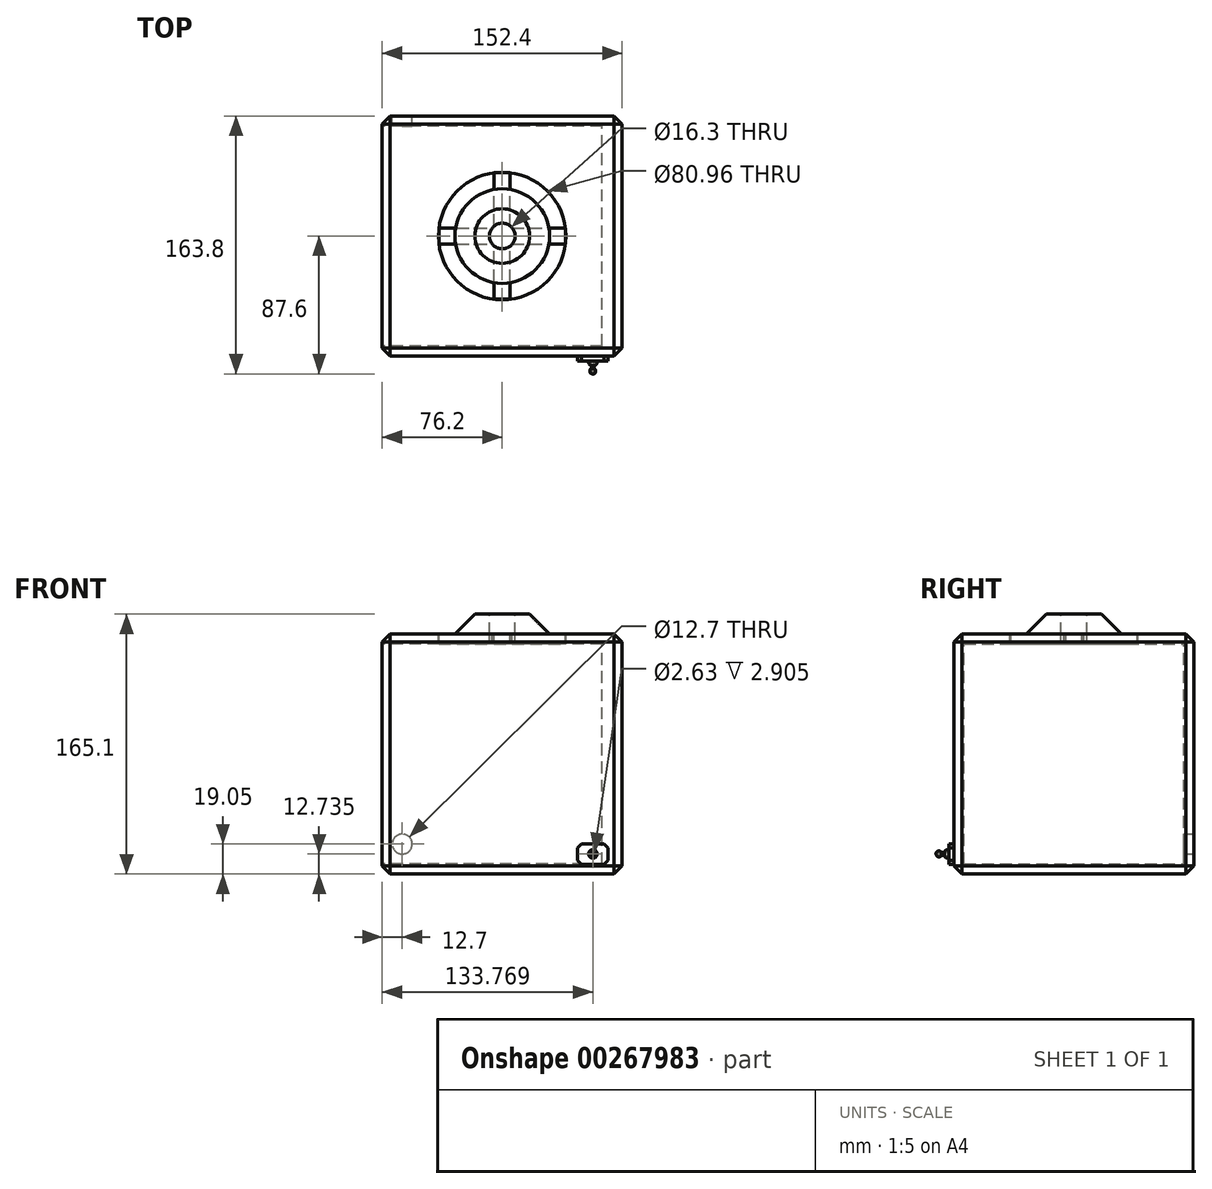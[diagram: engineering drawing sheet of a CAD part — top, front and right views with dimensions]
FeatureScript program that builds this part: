
annotation { "Feature Type Name" : "Feature", "Feature Type Description" : "" }
export const myFeature = defineFeature(function(context is Context, id is Id, definition is map)
    precondition{}
    {
        {
            var Q0;
            Q0=qCreatedBy(makeId("Top.planeOp"),FACE);
            var sketch = newSketch(context, id + "F0", { "sketchPlane" : qUnion([Q0])});
            skLineSegment(sketch, "E0.bottom", {"start": v(152.4, -152.4) * mm, "end": v(-152.4, -152.4) * mm});
            skLineSegment(sketch, "E0.top", {"start": v(152.4, 152.4) * mm, "end": v(-152.4, 152.4) * mm});
            skLineSegment(sketch, "E0.left", {"start": v(152.4, -152.4) * mm, "end": v(152.4, 152.4) * mm});
            skLineSegment(sketch, "E0.right", {"start": v(-152.4, -152.4) * mm, "end": v(-152.4, 152.4) * mm});
            skPoint(sketch, "E0.middle", {"position": v(0, 0) * mm});
            skSolve(sketch);
        }
        {
            var Q0;
            Q0=makeQuery(id+"F0.imprint","IMPRINT",FACE,{"disambiguationData":[TD([[makeQuery(id+"F0.imprint","IMPRINT",EDGE,{"derivedFrom":sQuery(id+"F0.wireOp",EDGE,"E0.bottom")}),-1.0]])]});
            extrude(context, id + "F1", {"entities" : qUnion([Q0]), "depth" : 304.8 * mm});
        }
        {
            var Q0;
            Q0=makeQuery(id+"F1.opExtrude","CAP_FACE",FACE,{"disambiguationData":[OSD([sQuery(id+"F0.wireOp",EDGE,"E0.bottom"),sQuery(id+"F0.wireOp",EDGE,"E0.top"),sQuery(id+"F0.wireOp",EDGE,"E0.left"),sQuery(id+"F0.wireOp",EDGE,"E0.right")])],"isStart":false});
            var sketch = newSketch(context, id + "F2", { "sketchPlane" : qUnion([Q0])});
            skCircle(sketch, "E1", {"center": v(0, 0) * mm, "radius": 80.96 * mm});
            skSolve(sketch);
        }
        {
            var Q0;
            Q0=makeQuery(id+"F1.opExtrude","SWEPT_FACE",FACE,{"disambiguationData":[OSD([sQuery(id+"F0.wireOp",EDGE,"E0.right")])]});
            var sketch = newSketch(context, id + "F3", { "sketchPlane" : qUnion([Q0])});
            skLineSegment(sketch, "E2.bottom", {"start": v(139.7, 12.7) * mm, "end": v(-139.7, 12.7) * mm});
            skLineSegment(sketch, "E2.top", {"start": v(139.7, 292.1) * mm, "end": v(-139.7, 292.1) * mm});
            skLineSegment(sketch, "E2.left", {"start": v(139.7, 12.7) * mm, "end": v(139.7, 292.1) * mm});
            skLineSegment(sketch, "E2.right", {"start": v(-139.7, 12.7) * mm, "end": v(-139.7, 292.1) * mm});
            skPoint(sketch, "E2.middle", {"position": v(0, 152.4) * mm});
            skSolve(sketch);
        }
        {
            var Q0;
            Q0=makeQuery(id+"F3.imprint","IMPRINT",FACE,{"disambiguationData":[TD([[makeQuery(id+"F3.imprint","IMPRINT",EDGE,{"derivedFrom":sQuery(id+"F3.wireOp",EDGE,"E2.bottom")}),-1.0]])]});
            extrude(context, id + "F4", {"entities" : qUnion([Q0]), "operationType" : NewBodyOperationType.REMOVE, "oppositeDirection" : true, "depth" : 279.4 * mm});
        }
        {
            var Q0;
            Q0=makeQuery(id+"F2.imprint","IMPRINT",FACE,{"disambiguationData":[TD([[makeQuery(id+"F2.imprint","IMPRINT",EDGE,{"derivedFrom":sQuery(id+"F2.wireOp",EDGE,"E1")}),1.0]])]});
            extrude(context, id + "F5", {"entities" : qUnion([Q0]), "operationType" : NewBodyOperationType.REMOVE, "oppositeDirection" : true, "depth" : 25.4 * mm});
        }
        {
            var Q0;
            Q0=makeQuery(id+"F1.opExtrude","SWEPT_FACE",FACE,{"disambiguationData":[OSD([sQuery(id+"F0.wireOp",EDGE,"E0.top")])]});
            var sketch = newSketch(context, id + "F6", { "sketchPlane" : qUnion([Q0])});
            skCircle(sketch, "E3", {"center": v(127, 38.1) * mm, "radius": 12.7 * mm});
            skSolve(sketch);
        }
        {
            var Q0;
            Q0=makeQuery(id+"F1.opExtrude","CAP_FACE",FACE,{"disambiguationData":[OSD([sQuery(id+"F0.wireOp",EDGE,"E0.bottom"),sQuery(id+"F0.wireOp",EDGE,"E0.top"),sQuery(id+"F0.wireOp",EDGE,"E0.left"),sQuery(id+"F0.wireOp",EDGE,"E0.right")])],"isStart":false});
            var sketch = newSketch(context, id + "F7", { "sketchPlane" : qUnion([Q0])});
            skCircle(sketch, "E4", {"center": v(0, 0) * mm, "radius": 60.08 * mm});
            skSolve(sketch);
        }
        {
            var Q0;
            Q0 = qSketchRegion(id + "F6", true);
            extrude(context, id + "F8", {"entities" : qUnion([Q0]), "operationType" : NewBodyOperationType.REMOVE, "endBound" : BoundingType.UP_TO_NEXT, "oppositeDirection" : true, "depth" : 25.4 * mm});
        }
        {
            var Q0;
            Q0=makeQuery(id+"F1.opExtrude","SWEPT_FACE",FACE,{"disambiguationData":[OSD([sQuery(id+"F0.wireOp",EDGE,"E0.bottom")])]});
            var sketch = newSketch(context, id + "F9", { "sketchPlane" : qUnion([Q0])});
            skLineSegment(sketch, "E5.bottom", {"start": v(134.19, 38.44) * mm, "end": v(95.34, 38.44) * mm});
            skLineSegment(sketch, "E5.top", {"start": v(134.19, 12.14) * mm, "end": v(95.34, 12.14) * mm});
            skLineSegment(sketch, "E5.left", {"start": v(134.19, 38.44) * mm, "end": v(134.19, 12.14) * mm});
            skLineSegment(sketch, "E5.right", {"start": v(95.34, 38.44) * mm, "end": v(95.34, 12.14) * mm});
            skSolve(sketch);
        }
        {
            var Q0;
            Q0 = qSketchRegion(id + "F9", true);
            extrude(context, id + "F10", {"entities" : qUnion([Q0]), "operationType" : NewBodyOperationType.ADD, "depth" : 6.35 * mm});
        }
        {
            var Q0;
            Q0=makeQuery(id+"F7.imprint","IMPRINT",FACE,{"disambiguationData":[TD([[makeQuery(id+"F7.imprint","IMPRINT",EDGE,{"derivedFrom":sQuery(id+"F7.wireOp",EDGE,"E4")}),1.0]])]});
            extrude(context, id + "F11", {"entities" : qUnion([Q0]), "depth" : 25.4 * mm});
        }
        {
            var Q0;
            Q0=makeQuery(id+"F10.opExtrude","SWEPT_EDGE",EDGE,{"disambiguationData":[OSD([sQuery(id+"F9.wireOp",EDGE,"E5.bottom"),sQuery(id+"F9.wireOp",EDGE,"E5.right")])]});
            var Q1;
            Q1=makeQuery(id+"F10.opExtrude","SWEPT_EDGE",EDGE,{"disambiguationData":[OSD([sQuery(id+"F9.wireOp",EDGE,"E5.top"),sQuery(id+"F9.wireOp",EDGE,"E5.left")])]});
            var Q2;
            Q2=makeQuery(id+"F10.opExtrude","SWEPT_EDGE",EDGE,{"disambiguationData":[OSD([sQuery(id+"F9.wireOp",EDGE,"E5.bottom"),sQuery(id+"F9.wireOp",EDGE,"E5.left")])]});
            var Q3;
            Q3=makeQuery(id+"F10.opExtrude","SWEPT_EDGE",EDGE,{"disambiguationData":[OSD([sQuery(id+"F9.wireOp",EDGE,"E5.top"),sQuery(id+"F9.wireOp",EDGE,"E5.right")])]});
            chamfer(context, id + "F12", {"entities" : qUnion([Q0, Q1, Q2, Q3]), "width" : 5.08 * mm, "tangentPropagation" : true});
        }
        {
            var Q0;
            Q0=makeQuery(id+"F11.opExtrude","CAP_FACE",FACE,{"disambiguationData":[OSD([sQuery(id+"F7.wireOp",EDGE,"E4")])],"isStart":false});
            chamfer(context, id + "F13", {"entities" : qUnion([Q0]), "width" : 25.4 * mm, "tangentPropagation" : true});
        }
        {
            var Q0;
            Q0=makeQuery(id+"F1.opExtrude","CAP_FACE",FACE,{"disambiguationData":[OSD([sQuery(id+"F0.wireOp",EDGE,"E0.bottom"),sQuery(id+"F0.wireOp",EDGE,"E0.top"),sQuery(id+"F0.wireOp",EDGE,"E0.left"),sQuery(id+"F0.wireOp",EDGE,"E0.right")])],"isStart":false});
            var sketch = newSketch(context, id + "F14", { "sketchPlane" : qUnion([Q0])});
            skLineSegment(sketch, "E6.bottom", {"start": v(10.16, -80.32) * mm, "end": v(-10.16, -80.32) * mm});
            skLineSegment(sketch, "E6.top", {"start": v(10.16, 80.32) * mm, "end": v(-10.16, 80.32) * mm});
            skLineSegment(sketch, "E6.left", {"start": v(10.16, -80.32) * mm, "end": v(10.16, 80.32) * mm});
            skLineSegment(sketch, "E6.right", {"start": v(-10.16, -80.32) * mm, "end": v(-10.16, 80.32) * mm});
            skPoint(sketch, "E6.middle", {"position": v(0, 0) * mm});
            skSolve(sketch);
        }
        {
            var Q0;
            Q0 = qSketchRegion(id + "F14", true);
            extrude(context, id + "F15", {"entities" : qUnion([Q0]), "oppositeDirection" : true, "depth" : 12.7 * mm});
        }
        {
            var Q0;
            Q0=makeQuery(id+"F1.opExtrude","CAP_FACE",FACE,{"disambiguationData":[OSD([sQuery(id+"F0.wireOp",EDGE,"E0.bottom"),sQuery(id+"F0.wireOp",EDGE,"E0.top"),sQuery(id+"F0.wireOp",EDGE,"E0.left"),sQuery(id+"F0.wireOp",EDGE,"E0.right")])],"isStart":false});
            var sketch = newSketch(context, id + "F16", { "sketchPlane" : qUnion([Q0])});
            skLineSegment(sketch, "E7.bottom", {"start": v(-80.32, 10.16) * mm, "end": v(80.32, 10.16) * mm});
            skLineSegment(sketch, "E7.top", {"start": v(-80.32, -10.16) * mm, "end": v(80.32, -10.16) * mm});
            skLineSegment(sketch, "E7.left", {"start": v(-80.32, 10.16) * mm, "end": v(-80.32, -10.16) * mm});
            skLineSegment(sketch, "E7.right", {"start": v(80.32, 10.16) * mm, "end": v(80.32, -10.16) * mm});
            skPoint(sketch, "E7.middle", {"position": v(0, 0) * mm});
            skSolve(sketch);
        }
        {
            var Q0;
            Q0=makeQuery(id+"F16.imprint","IMPRINT",FACE,{"disambiguationData":[TD([[makeQuery(id+"F16.imprint","IMPRINT",EDGE,{"derivedFrom":sQuery(id+"F16.wireOp",EDGE,"E7.bottom")}),-1.0]])]});
            extrude(context, id + "F17", {"entities" : qUnion([Q0]), "oppositeDirection" : true, "depth" : 12.7 * mm});
        }
        {
            var Q0;
            Q0=makeQuery(id+"F10.opExtrude","CAP_FACE",FACE,{"disambiguationData":[OSD([sQuery(id+"F9.wireOp",EDGE,"E5.bottom"),sQuery(id+"F9.wireOp",EDGE,"E5.top"),sQuery(id+"F9.wireOp",EDGE,"E5.left"),sQuery(id+"F9.wireOp",EDGE,"E5.right")])],"isStart":false});
            var sketch = newSketch(context, id + "F18", { "sketchPlane" : qUnion([Q0])});
            skCircle(sketch, "E8", {"center": v(115.14, 25.47) * mm, "radius": 5.43 * mm});
            skSolve(sketch);
        }
        {
            var Q0;
            Q0=makeQuery(id+"F18.imprint","IMPRINT",FACE,{"disambiguationData":[TD([[makeQuery(id+"F18.imprint","IMPRINT",EDGE,{"derivedFrom":sQuery(id+"F18.wireOp",EDGE,"E8")}),1.0]])]});
            var Q1;
            Q1=sQuery(id+"F18.wireOp",EDGE,"E8");
            extrude(context, id + "F19", {"entities" : qUnion([Q0]), "operationType" : NewBodyOperationType.ADD, "surfaceEntities" : qUnion([Q1]), "depth" : 6.35 * mm});
        }
        {
            var Q0;
            Q0=makeQuery(id+"F19.opExtrude","CAP_EDGE",EDGE,{"disambiguationData":[OSD([sQuery(id+"F18.wireOp",EDGE,"E8")])],"isStart":false});
            fillet(context, id + "F20", {"entities" : qUnion([Q0]), "radius" : 5.08 * mm, "tangentPropagation" : true, "allowEdgeOverflow" : false});
        }
        {
            var Q0;
            Q0=makeQuery(id+"F19.opExtrude","CAP_FACE",FACE,{"disambiguationData":[OSD([sQuery(id+"F18.wireOp",EDGE,"E8")])],"isStart":false});
            var sketch = newSketch(context, id + "F21", { "sketchPlane" : qUnion([Q0])});
            skCircle(sketch, "E9", {"center": v(115.14, 25.47) * mm, "radius": 2.63 * mm});
            skSolve(sketch);
        }
        {
            var Q0;
            Q0 = qSketchRegion(id + "F21", true);
            extrude(context, id + "F22", {"entities" : qUnion([Q0]), "operationType" : NewBodyOperationType.REMOVE, "oppositeDirection" : true, "depth" : 6.35 * mm});
        }
        {
            var Q0;
            Q0=makeQuery(id+"F18.imprint","IMPRINT",FACE,{"disambiguationData":[TD([[makeQuery(id+"F18.imprint","IMPRINT",EDGE,{"derivedFrom":sQuery(id+"F18.wireOp",EDGE,"E8")}),1.0]])]});
            var sketch = newSketch(context, id + "F23", { "sketchPlane" : qUnion([Q0])});
            skCircle(sketch, "E10", {"center": v(115.02, 25.55) * mm, "radius": 1.82 * mm});
            skSolve(sketch);
        }
        {
            var Q0;
            Q0 = qSketchRegion(id + "F23", true);
            extrude(context, id + "F24", {"entities" : qUnion([Q0]), "operationType" : NewBodyOperationType.ADD, "depth" : 12.7 * mm});
        }
        {
            var Q0;
            Q0=makeQuery(id+"F24.opExtrude","CAP_FACE",FACE,{"disambiguationData":[OSD([sQuery(id+"F23.wireOp",EDGE,"E10")])],"isStart":false});
            var sketch = newSketch(context, id + "F25", { "sketchPlane" : qUnion([Q0])});
            skLineSegment(sketch, "E11", {"start": v(115.02, 25.55) * mm, "end": v(115.02, 29.24) * mm});
            skLineSegment(sketch, "E12", {"start": v(115.02, 29.24) * mm, "end": v(115.02, 21.87) * mm});
            skArc(sketch, "E13", {"start": v(115.02, 21.87) * mm, "mid": v(118.65, 25.55) * mm, "end": v(115.02, 29.24) * mm});
            skSolve(sketch);
        }
        {
            var Q0;
            {var subQ0=sQuery(id+"F25.wireOp",EDGE,"E13");Q0=makeQuery(id+"F25.imprint","IMPRINT",FACE,{"disambiguationData":[TD([[makeQuery(id+"F25.imprint","IMPRINT",EDGE,{"derivedFrom":subQ0}),1.0]])]});}
            var Q1;
            Q1=sQuery(id+"F25.wireOp",EDGE,"E12");
            revolve(context, id + "F26", {"operationType" : NewBodyOperationType.ADD, "entities" : qUnion([Q0]), "axis" : qUnion([Q1]), "revolveType" : RevolveType.FULL});
        }
        {
            var Q0;
            Q0=makeQuery(id+"F1.opExtrude","SWEPT_BODY",BODY,{"disambiguationData":[OSD([sQuery(id+"F0.wireOp",EDGE,"E0.bottom"),sQuery(id+"F0.wireOp",EDGE,"E0.top"),sQuery(id+"F0.wireOp",EDGE,"E0.left"),sQuery(id+"F0.wireOp",EDGE,"E0.right")])]});
            var Q1;
            Q1=makeQuery(id+"F17.opExtrude","SWEPT_BODY",BODY,{"disambiguationData":[OSD([sQuery(id+"F16.wireOp",EDGE,"E7.bottom"),sQuery(id+"F16.wireOp",EDGE,"E7.top"),sQuery(id+"F16.wireOp",EDGE,"E7.left"),sQuery(id+"F16.wireOp",EDGE,"E7.right")])]});
            var Q2;
            Q2=makeQuery(id+"F15.opExtrude","SWEPT_BODY",BODY,{"disambiguationData":[OSD([sQuery(id+"F14.wireOp",EDGE,"E6.bottom"),sQuery(id+"F14.wireOp",EDGE,"E6.top"),sQuery(id+"F14.wireOp",EDGE,"E6.left"),sQuery(id+"F14.wireOp",EDGE,"E6.right")])]});
            var Q3;
            Q3=makeQuery(id+"F11.opExtrude","SWEPT_BODY",BODY,{"disambiguationData":[OSD([sQuery(id+"F7.wireOp",EDGE,"E4")])]});
            var Q4;
            Q4=makeQuery(id+"F1.opExtrude","CAP_VERTEX",VERTEX,{"disambiguationData":[OSD([sQuery(id+"F0.wireOp",EDGE,"E0.top"),sQuery(id+"F0.wireOp",EDGE,"E0.right")])],"isStart":false});
            transform(context, id + "F27", {"entities" : qUnion([Q0, Q1, Q2, Q3]), "transformType" : TransformType.SCALE_UNIFORMLY, "scale" : .5, "scalePoint" : qUnion([Q4]), "makeCopy" : false});
        }
        {
            var Q0;
            Q0=makeQuery(id+"F11.opExtrude","SWEPT_BODY",BODY,{"disambiguationData":[OSD([sQuery(id+"F7.wireOp",EDGE,"E4")])]});
            var Q1;
            Q1=makeQuery(id+"F1.opExtrude","SWEPT_BODY",BODY,{"disambiguationData":[OSD([sQuery(id+"F0.wireOp",EDGE,"E0.bottom"),sQuery(id+"F0.wireOp",EDGE,"E0.top"),sQuery(id+"F0.wireOp",EDGE,"E0.left"),sQuery(id+"F0.wireOp",EDGE,"E0.right")])]});
            var Q2;
            Q2=makeQuery(id+"F15.opExtrude","SWEPT_BODY",BODY,{"disambiguationData":[OSD([sQuery(id+"F14.wireOp",EDGE,"E6.bottom"),sQuery(id+"F14.wireOp",EDGE,"E6.top"),sQuery(id+"F14.wireOp",EDGE,"E6.left"),sQuery(id+"F14.wireOp",EDGE,"E6.right")])]});
            var Q3;
            Q3=makeQuery(id+"F17.opExtrude","SWEPT_BODY",BODY,{"disambiguationData":[OSD([sQuery(id+"F16.wireOp",EDGE,"E7.bottom"),sQuery(id+"F16.wireOp",EDGE,"E7.top"),sQuery(id+"F16.wireOp",EDGE,"E7.left"),sQuery(id+"F16.wireOp",EDGE,"E7.right")])]});
            var Q4;
            Q4=qCreatedBy(makeId("Origin.pointOp"),VERTEX);
            var Q5;
            Q5=qCreatedBy(makeId("Origin.pointOp"),VERTEX);
            transform(context, id + "F28", {"entities" : qUnion([Q0, Q1, Q2, Q3]), "transformType" : TransformType.TRANSLATION_3D, "dx" : 81.28 * mm, "dy" : -76.2 * mm, "dz" : -231.14 * mm, "makeCopy" : false});
        }
        {
            var Q0;
            Q0=makeQuery(id+"F11.opExtrude","CAP_FACE",FACE,{"disambiguationData":[OSD([sQuery(id+"F7.wireOp",EDGE,"E4")])],"isStart":false});
            var sketch = newSketch(context, id + "F29", { "sketchPlane" : qUnion([Q0])});
            skCircle(sketch, "E14", {"center": v(5.08, 0) * mm, "radius": 8.15 * mm});
            skSolve(sketch);
        }
        {
            var Q0;
            Q0 = qSketchRegion(id + "F29", true);
            extrude(context, id + "F30", {"entities" : qUnion([Q0]), "operationType" : NewBodyOperationType.REMOVE, "oppositeDirection" : true, "depth" : 127 * mm});
        }
        {
            var Q0;
            Q0=makeQuery(id+"F1.opExtrude","CAP_EDGE",EDGE,{"disambiguationData":[OSD([sQuery(id+"F0.wireOp",EDGE,"E0.left")])],"isStart":false});
            var Q1;
            Q1=makeQuery(id+"F1.opExtrude","CAP_EDGE",EDGE,{"disambiguationData":[OSD([sQuery(id+"F0.wireOp",EDGE,"E0.bottom")])],"isStart":false});
            var Q2;
            Q2=makeQuery(id+"F1.opExtrude","CAP_EDGE",EDGE,{"disambiguationData":[OSD([sQuery(id+"F0.wireOp",EDGE,"E0.right")])],"isStart":false});
            var Q3;
            Q3=makeQuery(id+"F1.opExtrude","CAP_EDGE",EDGE,{"disambiguationData":[OSD([sQuery(id+"F0.wireOp",EDGE,"E0.top")])],"isStart":false});
            var Q4;
            Q4=makeQuery(id+"F1.opExtrude","SWEPT_EDGE",EDGE,{"disambiguationData":[OSD([sQuery(id+"F0.wireOp",EDGE,"E0.top"),sQuery(id+"F0.wireOp",EDGE,"E0.right")])]});
            var Q5;
            Q5=makeQuery(id+"F1.opExtrude","SWEPT_EDGE",EDGE,{"disambiguationData":[OSD([sQuery(id+"F0.wireOp",EDGE,"E0.top"),sQuery(id+"F0.wireOp",EDGE,"E0.left")])]});
            var Q6;
            Q6=makeQuery(id+"F1.opExtrude","CAP_EDGE",EDGE,{"disambiguationData":[OSD([sQuery(id+"F0.wireOp",EDGE,"E0.top")])],"isStart":true});
            var Q7;
            Q7=makeQuery(id+"F1.opExtrude","SWEPT_EDGE",EDGE,{"disambiguationData":[OSD([sQuery(id+"F0.wireOp",EDGE,"E0.bottom"),sQuery(id+"F0.wireOp",EDGE,"E0.left")])]});
            var Q8;
            Q8=makeQuery(id+"F1.opExtrude","CAP_EDGE",EDGE,{"disambiguationData":[OSD([sQuery(id+"F0.wireOp",EDGE,"E0.left")])],"isStart":true});
            var Q9;
            Q9=makeQuery(id+"F1.opExtrude","CAP_EDGE",EDGE,{"disambiguationData":[OSD([sQuery(id+"F0.wireOp",EDGE,"E0.bottom")])],"isStart":true});
            var Q10;
            Q10=makeQuery(id+"F1.opExtrude","SWEPT_EDGE",EDGE,{"disambiguationData":[OSD([sQuery(id+"F0.wireOp",EDGE,"E0.bottom"),sQuery(id+"F0.wireOp",EDGE,"E0.right")])]});
            var Q11;
            Q11=makeQuery(id+"F1.opExtrude","CAP_EDGE",EDGE,{"disambiguationData":[OSD([sQuery(id+"F0.wireOp",EDGE,"E0.right")])],"isStart":true});
            chamfer(context, id + "F31", {"entities" : qUnion([Q0, Q1, Q2, Q3, Q4, Q5, Q6, Q7, Q8, Q9, Q10, Q11]), "width" : 5.08 * mm, "tangentPropagation" : true});
        }
    });
